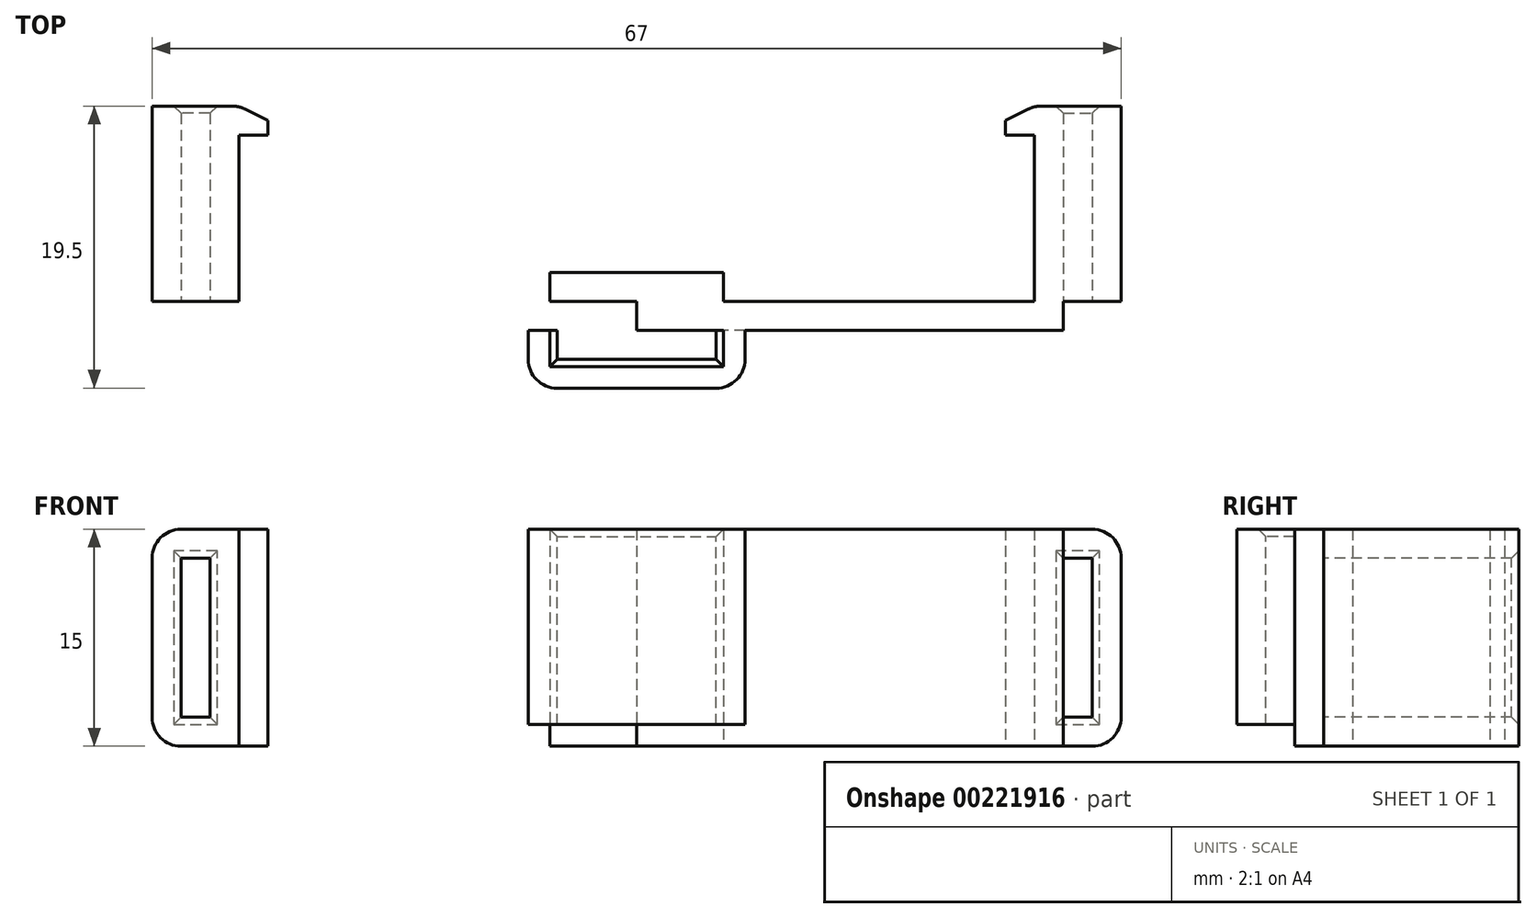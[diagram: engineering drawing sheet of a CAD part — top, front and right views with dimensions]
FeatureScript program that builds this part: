
annotation { "Feature Type Name" : "Feature", "Feature Type Description" : "" }
export const myFeature = defineFeature(function(context is Context, id is Id, definition is map)
    precondition{}
    {
        {
            var Q0;
            Q0=qCreatedBy(makeId("Top.planeOp"),FACE);
            var sketch = newSketch(context, id + "F0", { "sketchPlane" : qUnion([Q0])});
            skLineSegment(sketch, "E0.bottom", {"start": v(27.5, -1) * mm, "end": v(-27.5, -1) * mm});
            skLineSegment(sketch, "E0.top", {"start": v(27.5, 1) * mm, "end": v(-27.5, 1) * mm});
            skLineSegment(sketch, "E0.left", {"start": v(27.5, -1) * mm, "end": v(27.5, 1) * mm});
            skLineSegment(sketch, "E0.right", {"start": v(-27.5, -1) * mm, "end": v(-27.5, 1) * mm});
            skPoint(sketch, "E0.middle", {"position": v(0, 0) * mm});
            skLineSegment(sketch, "E1.bottom", {"start": v(-27.5, -1) * mm, "end": v(-29.5, -1) * mm});
            skLineSegment(sketch, "E1.top", {"start": v(-27.5, 10.5) * mm, "end": v(-29.5, 10.5) * mm});
            skLineSegment(sketch, "E1.left", {"start": v(-27.5, -1) * mm, "end": v(-27.5, 10.5) * mm});
            skLineSegment(sketch, "E1.right", {"start": v(-29.5, -1) * mm, "end": v(-29.5, 10.5) * mm});
            skLineSegment(sketch, "E2.bottom", {"start": v(27.5, -1) * mm, "end": v(29.5, -1) * mm});
            skLineSegment(sketch, "E2.top", {"start": v(27.5, 10.5) * mm, "end": v(29.5, 10.5) * mm});
            skLineSegment(sketch, "E2.left", {"start": v(27.5, -1) * mm, "end": v(27.5, 10.5) * mm});
            skLineSegment(sketch, "E2.right", {"start": v(29.5, -1) * mm, "end": v(29.5, 10.5) * mm});
            skLineSegment(sketch, "E3", {"start": v(27.5, 1) * mm, "end": v(27.5, 10.5) * mm});
            skLineSegment(sketch, "E4", {"start": v(-27.5, 1) * mm, "end": v(-27.5, 10.5) * mm});
            skLineSegment(sketch, "E5.bottom", {"start": v(-29.5, 10.5) * mm, "end": v(-25.5, 10.5) * mm});
            skLineSegment(sketch, "E5.top", {"start": v(-29.5, 12.5) * mm, "end": v(-25.5, 12.5) * mm});
            skLineSegment(sketch, "E5.left", {"start": v(-29.5, 10.5) * mm, "end": v(-29.5, 12.5) * mm});
            skLineSegment(sketch, "E5.right", {"start": v(-25.5, 10.5) * mm, "end": v(-25.5, 12.5) * mm});
            skLineSegment(sketch, "E6.bottom", {"start": v(29.5, 10.5) * mm, "end": v(25.5, 10.5) * mm});
            skLineSegment(sketch, "E6.top", {"start": v(29.5, 12.5) * mm, "end": v(25.5, 12.5) * mm});
            skLineSegment(sketch, "E6.left", {"start": v(29.5, 10.5) * mm, "end": v(29.5, 12.5) * mm});
            skLineSegment(sketch, "E6.right", {"start": v(25.5, 10.5) * mm, "end": v(25.5, 12.5) * mm});
            skLineSegment(sketch, "E7", {"start": v(-25.5, 11.5) * mm, "end": v(-27.5, 12.5) * mm});
            skLineSegment(sketch, "E8", {"start": v(25.5, 11.5) * mm, "end": v(27.5, 12.5) * mm});
            skLineSegment(sketch, "E9", {"start": v(0, 0) * mm, "end": v(0, 17.19) * mm, "construction": true});
            skPoint(sketch, "E9.endSnap0", {"position": v(0, 1) * mm});
            skLineSegment(sketch, "E10.bottom", {"start": v(-29.5, 12.5) * mm, "end": v(-33.5, 12.5) * mm});
            skLineSegment(sketch, "E10.top", {"start": v(-29.5, -1) * mm, "end": v(-33.5, -1) * mm});
            skLineSegment(sketch, "E10.left", {"start": v(-29.5, 12.5) * mm, "end": v(-29.5, -1) * mm});
            skLineSegment(sketch, "E10.right", {"start": v(-33.5, 12.5) * mm, "end": v(-33.5, -1) * mm});
            skLineSegment(sketch, "E11.MirrorCS", {"start": v(33.5, 12.5) * mm, "end": v(33.5, -1) * mm});
            skLineSegment(sketch, "E12.MirrorCS", {"start": v(29.5, 12.5) * mm, "end": v(29.5, -1) * mm});
            skLineSegment(sketch, "E13.MirrorCS", {"start": v(29.5, -1) * mm, "end": v(33.5, -1) * mm});
            skLineSegment(sketch, "E14.MirrorCS", {"start": v(29.5, 12.5) * mm, "end": v(33.5, 12.5) * mm});
            skPoint(sketch, "E15.oppositeSnap0", {"position": v(0, -1) * mm});
            skLineSegment(sketch, "E15.bottom", {"start": v(-29.5, -1) * mm, "end": v(0, -1) * mm});
            skLineSegment(sketch, "E15.top", {"start": v(-29.5, -3) * mm, "end": v(0, -3) * mm});
            skLineSegment(sketch, "E15.left", {"start": v(-29.5, -1) * mm, "end": v(-29.5, -3) * mm});
            skLineSegment(sketch, "E15.right", {"start": v(0, -1) * mm, "end": v(0, -3) * mm});
            skLineSegment(sketch, "E16.MirrorCS", {"start": v(-27.5, -1) * mm, "end": v(27.5, -1) * mm});
            skLineSegment(sketch, "E17.MirrorCS", {"start": v(29.5, -3) * mm, "end": v(0, -3) * mm});
            skLineSegment(sketch, "E18.MirrorCS", {"start": v(29.5, -1) * mm, "end": v(29.5, -3) * mm});
            skLineSegment(sketch, "E19.MirrorCS", {"start": v(29.5, -1) * mm, "end": v(0, -1) * mm});
            skLineSegment(sketch, "E20.bottom", {"start": v(-22, 1) * mm, "end": v(-6, 1) * mm});
            skLineSegment(sketch, "E20.top", {"start": v(-22, -1) * mm, "end": v(-6, -1) * mm});
            skLineSegment(sketch, "E20.left", {"start": v(-22, 1) * mm, "end": v(-22, -1) * mm});
            skLineSegment(sketch, "E20.right", {"start": v(-6, 1) * mm, "end": v(-6, -1) * mm});
            skLineSegment(sketch, "E21.MirrorCS", {"start": v(22, 1) * mm, "end": v(22, -1) * mm});
            skLineSegment(sketch, "E22.MirrorCS", {"start": v(22, 1) * mm, "end": v(6, 1) * mm});
            skLineSegment(sketch, "E23.MirrorCS", {"start": v(6, 1) * mm, "end": v(6, -1) * mm});
            skLineSegment(sketch, "E24.MirrorCS", {"start": v(22, -1) * mm, "end": v(6, -1) * mm});
            skSolve(sketch);
        }
        {
            var Q0;
            Q0=makeQuery(id+"F0.imprint","IMPRINT",FACE,{"disambiguationData":[TD([[makeQuery(id+"F0.imprint","IMPRINT",EDGE,{"derivedFrom":sQuery(id+"F0.wireOp",EDGE,"E0.bottom")}),-1.0]])]});
            var Q1;
            Q1=makeQuery(id+"F0.imprint","IMPRINT",FACE,{"disambiguationData":[TD([[makeQuery(id+"F0.imprint","IMPRINT",EDGE,{"derivedFrom":sQuery(id+"F0.wireOp",EDGE,"E1.bottom")}),-1.0]])]});
            var Q2;
            Q2=makeQuery(id+"F0.imprint","IMPRINT",FACE,{"disambiguationData":[TD([[makeQuery(id+"F0.imprint","IMPRINT",EDGE,{"derivedFrom":sQuery(id+"F0.wireOp",EDGE,"E2.bottom")}),1.0]])]});
            var Q3;
            {var subQ0=sQuery(id+"F0.wireOp",EDGE,"E5.left");Q3=makeQuery(id+"F0.imprint","IMPRINT",FACE,{"disambiguationData":[TD([[makeQuery(id+"F0.imprint","IMPRINT",EDGE,{"derivedFrom":subQ0}),-1.0]])]});}
            var Q4;
            {var subQ0=sQuery(id+"F0.wireOp",EDGE,"E6.left");Q4=makeQuery(id+"F0.imprint","IMPRINT",FACE,{"disambiguationData":[TD([[makeQuery(id+"F0.imprint","IMPRINT",EDGE,{"derivedFrom":subQ0}),1.0]])]});}
            var Q5;
            {var subQ3=sQuery(id+"F0.wireOp",EDGE,"E10.bottom");Q5=makeQuery(id+"F0.imprint","IMPRINT",FACE,{"disambiguationData":[TD([[makeQuery(id+"F0.imprint","IMPRINT",EDGE,{"derivedFrom":subQ3}),1.0]])]});}
            var Q6;
            {var subQ3=sQuery(id+"F0.wireOp",EDGE,"E7");Q6=makeQuery(id+"F0.imprint","IMPRINT",FACE,{"disambiguationData":[TD([[makeQuery(id+"F0.imprint","IMPRINT",EDGE,{"derivedFrom":subQ3}),1.0]])]});}
            var Q7;
            {var subQ3=sQuery(id+"F0.wireOp",EDGE,"E8");Q7=makeQuery(id+"F0.imprint","IMPRINT",FACE,{"disambiguationData":[TD([[makeQuery(id+"F0.imprint","IMPRINT",EDGE,{"derivedFrom":subQ3}),-1.0]])]});}
            var Q8;
            Q8=makeQuery(id+"F0.imprint","IMPRINT",FACE,{"disambiguationData":[TD([[makeQuery(id+"F0.imprint","IMPRINT",EDGE,{"derivedFrom":sQuery(id+"F0.wireOp",EDGE,"E11.MirrorCS")}),-1.0]])]});
            var Q9;
            Q9=makeQuery(id+"F0.imprint","IMPRINT",FACE,{"disambiguationData":[TD([[makeQuery(id+"F0.imprint","IMPRINT",EDGE,{"derivedFrom":sQuery(id+"F0.wireOp",EDGE,"E1.left")}),1.0]])]});
            var Q10;
            {var subQ3=sQuery(id+"F0.wireOp",EDGE,"E2.left");Q10=makeQuery(id+"F0.imprint","IMPRINT",FACE,{"disambiguationData":[TD([[makeQuery(id+"F0.imprint","IMPRINT",EDGE,{"derivedFrom":subQ3}),-1.0]])]});}
            var Q11;
            {var subQ0=sQuery(id+"F0.wireOp",EDGE,"E2.left");Q11=makeQuery(id+"F0.imprint","IMPRINT",FACE,{"disambiguationData":[TD([[makeQuery(id+"F0.imprint","IMPRINT",EDGE,{"derivedFrom":subQ0}),1.0]])]});}
            var Q12;
            {var subQ3=sQuery(id+"F0.wireOp",EDGE,"E15.right");Q12=makeQuery(id+"F0.imprint","IMPRINT",FACE,{"disambiguationData":[TD([[makeQuery(id+"F0.imprint","IMPRINT",EDGE,{"derivedFrom":subQ3}),1.0]])]});}
            var Q13;
            {var subQ0=sQuery(id+"F0.wireOp",EDGE,"E20.right");Q13=makeQuery(id+"F0.imprint","IMPRINT",FACE,{"disambiguationData":[TD([[makeQuery(id+"F0.imprint","IMPRINT",EDGE,{"derivedFrom":subQ0}),1.0]])]});}
            var Q14;
            {var subQ1=sQuery(id+"F0.wireOp",EDGE,"E15.bottom");Q14=makeQuery(id+"F0.imprint","IMPRINT",FACE,{"disambiguationData":[TD([[makeQuery(id+"F0.imprint","IMPRINT",EDGE,{"derivedFrom":subQ1}),-1.0]])]});}
            var Q15;
            {var subQ0=sQuery(id+"F0.wireOp",EDGE,"E1.left");Q15=makeQuery(id+"F0.imprint","IMPRINT",FACE,{"disambiguationData":[TD([[makeQuery(id+"F0.imprint","IMPRINT",EDGE,{"derivedFrom":subQ0}),-1.0]])]});}
            extrude(context, id + "F1", {"entities" : qUnion([Q0, Q1, Q2, Q3, Q4, Q5, Q6, Q7, Q8, Q9, Q10, Q11, Q12, Q13, Q14, Q15]), "depth" : 15 * mm});
        }
        {
            var Q0;
            Q0=makeQuery(id+"F1.opExtrude","SWEPT_FACE",FACE,{"disambiguationData":[OSD([sQuery(id+"F0.wireOp",EDGE,"E0.bottom"),sQuery(id+"F0.wireOp",EDGE,"E1.bottom"),sQuery(id+"F0.wireOp",EDGE,"E2.bottom"),sQuery(id+"F0.wireOp",EDGE,"E10.top"),sQuery(id+"F0.wireOp",EDGE,"E13.MirrorCS")])]});
            var sketch = newSketch(context, id + "F2", { "sketchPlane" : qUnion([Q0])});
            skLineSegment(sketch, "E25", {"start": v(-31.5, 0) * mm, "end": v(-31.5, 15) * mm, "construction": true});
            skLineSegment(sketch, "E26.bottom", {"start": v(-31.5, 13) * mm, "end": v(-29.5, 13) * mm});
            skLineSegment(sketch, "E26.top", {"start": v(-31.5, 2) * mm, "end": v(-29.5, 2) * mm});
            skLineSegment(sketch, "E26.left", {"start": v(-31.5, 13) * mm, "end": v(-31.5, 2) * mm});
            skLineSegment(sketch, "E26.right", {"start": v(-29.5, 13) * mm, "end": v(-29.5, 2) * mm});
            skLineSegment(sketch, "E27.MirrorCS", {"start": v(-31.5, 13) * mm, "end": v(-33.5, 13) * mm});
            skLineSegment(sketch, "E28.MirrorCS", {"start": v(-33.5, 13) * mm, "end": v(-33.5, 2) * mm});
            skLineSegment(sketch, "E29.MirrorCS", {"start": v(-31.5, 2) * mm, "end": v(-33.5, 2) * mm});
            skLineSegment(sketch, "E30", {"start": v(-31.5, 13) * mm, "end": v(-33.5, 13) * mm, "construction": true});
            skLineSegment(sketch, "E31", {"start": v(-31.5, 13) * mm, "end": v(-31.5, 15) * mm, "construction": true});
            skLineSegment(sketch, "E32", {"start": v(-31.5, 2) * mm, "end": v(-31.5, 0) * mm, "construction": true});
            skLineSegment(sketch, "E33.MirrorCS", {"start": v(31.5, 2) * mm, "end": v(31.5, 0) * mm, "construction": true});
            skLineSegment(sketch, "E34.MirrorCS", {"start": v(31.5, 13) * mm, "end": v(29.5, 13) * mm});
            skLineSegment(sketch, "E35.MirrorCS", {"start": v(31.5, 2) * mm, "end": v(33.5, 2) * mm});
            skLineSegment(sketch, "E36.MirrorCS", {"start": v(31.5, 13) * mm, "end": v(31.5, 15) * mm, "construction": true});
            skLineSegment(sketch, "E37.MirrorCS", {"start": v(31.5, 13) * mm, "end": v(31.5, 2) * mm});
            skLineSegment(sketch, "E38.MirrorCS", {"start": v(31.5, 13) * mm, "end": v(33.5, 13) * mm});
            skLineSegment(sketch, "E39.MirrorCS", {"start": v(33.5, 13) * mm, "end": v(33.5, 2) * mm});
            skLineSegment(sketch, "E40.MirrorCS", {"start": v(31.5, 2) * mm, "end": v(29.5, 2) * mm});
            skLineSegment(sketch, "E41.MirrorCS", {"start": v(31.5, 13) * mm, "end": v(33.5, 13) * mm, "construction": true});
            skLineSegment(sketch, "E42.MirrorCS", {"start": v(31.5, 0) * mm, "end": v(31.5, 15) * mm, "construction": true});
            skLineSegment(sketch, "E43.MirrorCS", {"start": v(29.5, 13) * mm, "end": v(29.5, 2) * mm});
            skSolve(sketch);
        }
        {
            var Q0;
            Q0=makeQuery(id+"F2.imprint","IMPRINT",FACE,{"disambiguationData":[TD([[makeQuery(id+"F2.imprint","IMPRINT",EDGE,{"derivedFrom":sQuery(id+"F2.wireOp",EDGE,"E26.bottom")}),-1.0]])]});
            var Q1;
            Q1=makeQuery(id+"F2.imprint","IMPRINT",FACE,{"disambiguationData":[TD([[makeQuery(id+"F2.imprint","IMPRINT",EDGE,{"derivedFrom":sQuery(id+"F2.wireOp",EDGE,"E34.MirrorCS")}),1.0]])]});
            extrude(context, id + "F3", {"entities" : qUnion([Q0, Q1]), "operationType" : NewBodyOperationType.REMOVE, "endBound" : BoundingType.THROUGH_ALL, "oppositeDirection" : true, "depth" : 25 * mm});
        }
        {
            var Q0;
            Q0=makeQuery(id+"F1.opExtrude","CAP_FACE",FACE,{"disambiguationData":[OSD([sQuery(id+"F0.wireOp",EDGE,"E0.top"),sQuery(id+"F0.wireOp",EDGE,"E3"),sQuery(id+"F0.wireOp",EDGE,"E4"),sQuery(id+"F0.wireOp",EDGE,"E5.bottom"),sQuery(id+"F0.wireOp",EDGE,"E5.top"),sQuery(id+"F0.wireOp",EDGE,"E5.right"),sQuery(id+"F0.wireOp",EDGE,"E6.bottom"),sQuery(id+"F0.wireOp",EDGE,"E6.top"),sQuery(id+"F0.wireOp",EDGE,"E6.right"),sQuery(id+"F0.wireOp",EDGE,"E7"),sQuery(id+"F0.wireOp",EDGE,"E8"),sQuery(id+"F0.wireOp",EDGE,"E10.bottom"),sQuery(id+"F0.wireOp",EDGE,"E10.top"),sQuery(id+"F0.wireOp",EDGE,"E10.right"),sQuery(id+"F0.wireOp",EDGE,"E11.MirrorCS"),sQuery(id+"F0.wireOp",EDGE,"E13.MirrorCS"),sQuery(id+"F0.wireOp",EDGE,"E14.MirrorCS"),sQuery(id+"F0.wireOp",EDGE,"E15.top"),sQuery(id+"F0.wireOp",EDGE,"E15.left"),sQuery(id+"F0.wireOp",EDGE,"E17.MirrorCS"),sQuery(id+"F0.wireOp",EDGE,"E18.MirrorCS"),sQuery(id+"F0.wireOp",EDGE,"E20.top"),sQuery(id+"F0.wireOp",EDGE,"E20.left"),sQuery(id+"F0.wireOp",EDGE,"E20.right"),sQuery(id+"F0.wireOp",EDGE,"E21.MirrorCS"),sQuery(id+"F0.wireOp",EDGE,"E23.MirrorCS"),sQuery(id+"F0.wireOp",EDGE,"E24.MirrorCS")])],"isStart":false});
            var sketch = newSketch(context, id + "F4", { "sketchPlane" : qUnion([Q0])});
            skLineSegment(sketch, "E44.bottom", {"start": v(7.5, -3) * mm, "end": v(-7.5, -3) * mm});
            skLineSegment(sketch, "E44.top", {"start": v(7.5, -7) * mm, "end": v(-7.5, -7) * mm});
            skLineSegment(sketch, "E44.left", {"start": v(7.5, -3) * mm, "end": v(7.5, -7) * mm});
            skLineSegment(sketch, "E44.right", {"start": v(-7.5, -3) * mm, "end": v(-7.5, -7) * mm});
            skPoint(sketch, "E45", {"position": v(0, -3) * mm});
            skLineSegment(sketch, "E46.bottom", {"start": v(-5.5, -3) * mm, "end": v(5.5, -3) * mm});
            skLineSegment(sketch, "E46.top", {"start": v(-5.5, -5) * mm, "end": v(5.5, -5) * mm});
            skLineSegment(sketch, "E46.left", {"start": v(-5.5, -3) * mm, "end": v(-5.5, -5) * mm});
            skLineSegment(sketch, "E46.right", {"start": v(5.5, -3) * mm, "end": v(5.5, -5) * mm});
            skLineSegment(sketch, "E47", {"start": v(-5.5, -5) * mm, "end": v(-7.5, -5) * mm});
            skLineSegment(sketch, "E48", {"start": v(-7.5, -5) * mm, "end": v(-5.5, -5) * mm, "construction": true});
            skLineSegment(sketch, "E49", {"start": v(-5.5, -5) * mm, "end": v(-5.5, -7) * mm, "construction": true});
            skSolve(sketch);
        }
        {
            var Q0;
            {var subQ3=sQuery(id+"F4.wireOp",EDGE,"E46.left");Q0=makeQuery(id+"F4.imprint","IMPRINT",FACE,{"disambiguationData":[TD([[makeQuery(id+"F4.imprint","IMPRINT",EDGE,{"derivedFrom":subQ3}),-1.0]])]});}
            var Q1;
            {var subQ1=sQuery(id+"F4.wireOp",EDGE,"E44.top");Q1=makeQuery(id+"F4.imprint","IMPRINT",FACE,{"disambiguationData":[TD([[makeQuery(id+"F4.imprint","IMPRINT",EDGE,{"derivedFrom":subQ1}),-1.0]])]});}
            extrude(context, id + "F5", {"entities" : qUnion([Q0, Q1]), "operationType" : NewBodyOperationType.ADD, "oppositeDirection" : true, "depth" : 13.5 * mm});
        }
        {
            var Q0;
            Q0=makeQuery(id+"F1.opExtrude","CAP_EDGE",EDGE,{"disambiguationData":[OSD([sQuery(id+"F0.wireOp",EDGE,"E11.MirrorCS")])],"isStart":false});
            var Q1;
            Q1=makeQuery(id+"F1.opExtrude","CAP_EDGE",EDGE,{"disambiguationData":[OSD([sQuery(id+"F0.wireOp",EDGE,"E10.right")])],"isStart":false});
            var Q2;
            Q2=makeQuery(id+"F1.opExtrude","CAP_EDGE",EDGE,{"disambiguationData":[OSD([sQuery(id+"F0.wireOp",EDGE,"E11.MirrorCS")])],"isStart":true});
            var Q3;
            Q3=makeQuery(id+"F1.opExtrude","CAP_EDGE",EDGE,{"disambiguationData":[OSD([sQuery(id+"F0.wireOp",EDGE,"E10.right")])],"isStart":true});
            var Q4;
            Q4=makeQuery(id+"F1.opExtrude","SWEPT_EDGE",EDGE,{"disambiguationData":[OSD([sQuery(id+"F0.wireOp",EDGE,"E5.top"),sQuery(id+"F0.wireOp",EDGE,"E7")])]});
            var Q5;
            Q5=makeQuery(id+"F1.opExtrude","SWEPT_EDGE",EDGE,{"disambiguationData":[OSD([sQuery(id+"F0.wireOp",EDGE,"E6.top"),sQuery(id+"F0.wireOp",EDGE,"E8")])]});
            var Q6;
            Q6=makeQuery(id+"F5.opExtrude","SWEPT_EDGE",EDGE,{"disambiguationData":[OSD([sQuery(id+"F4.wireOp",EDGE,"E44.top"),sQuery(id+"F4.wireOp",EDGE,"E44.right")])]});
            var Q7;
            Q7=makeQuery(id+"F5.opExtrude","SWEPT_EDGE",EDGE,{"disambiguationData":[OSD([sQuery(id+"F4.wireOp",EDGE,"E44.top"),sQuery(id+"F4.wireOp",EDGE,"E44.left")])]});
            fillet(context, id + "F6", {"entities" : qUnion([Q0, Q1, Q2, Q3, Q4, Q5, Q6, Q7]), "radius" : 2 * mm, "tangentPropagation" : true, "allowEdgeOverflow" : false});
        }
        {
            var Q0;
            Q0=makeQuery(id+"F3.boolean.opBoolean","COPY",EDGE,{"derivedFrom":makeQuery(id+"F3.opExtrude","CAP_EDGE",EDGE,{"disambiguationData":[OSD([sQuery(id+"F2.wireOp",EDGE,"E26.left")])],"isStart":true})});
            var Q1;
            Q1=makeQuery(id+"F3.boolean.opBoolean","COPY",EDGE,{"derivedFrom":makeQuery(id+"F3.opExtrude","CAP_EDGE",EDGE,{"disambiguationData":[OSD([sQuery(id+"F2.wireOp",EDGE,"E28.MirrorCS")])],"isStart":true})});
            var Q2;
            Q2=makeQuery(id+"F3.boolean.opBoolean","COPY",EDGE,{"derivedFrom":makeQuery(id+"F3.opExtrude","CAP_EDGE",EDGE,{"disambiguationData":[OSD([sQuery(id+"F2.wireOp",EDGE,"E27.MirrorCS")])],"isStart":true})});
            var Q3;
            Q3=makeQuery(id+"F3.boolean.opBoolean","COPY",EDGE,{"derivedFrom":makeQuery(id+"F3.opExtrude","CAP_EDGE",EDGE,{"disambiguationData":[OSD([sQuery(id+"F2.wireOp",EDGE,"E29.MirrorCS")])],"isStart":true})});
            var Q4;
            Q4=makeQuery(id+"F3.boolean.opBoolean","COPY",EDGE,{"derivedFrom":makeQuery(id+"F3.opExtrude","CAP_EDGE",EDGE,{"disambiguationData":[OSD([sQuery(id+"F2.wireOp",EDGE,"E26.right")])],"isStart":true})});
            var Q5;
            Q5=makeQuery(id+"F3.boolean.opBoolean","COPY",EDGE,{"derivedFrom":makeQuery(id+"F3.opExtrude","CAP_EDGE",EDGE,{"disambiguationData":[OSD([sQuery(id+"F2.wireOp",EDGE,"E26.bottom")])],"isStart":true})});
            var Q6;
            Q6=makeQuery(id+"F3.boolean.opBoolean","COPY",EDGE,{"derivedFrom":makeQuery(id+"F3.opExtrude","CAP_EDGE",EDGE,{"disambiguationData":[OSD([sQuery(id+"F2.wireOp",EDGE,"E26.left")])],"isStart":true})});
            var Q7;
            Q7=makeQuery(id+"F3.boolean.opBoolean","COPY",EDGE,{"derivedFrom":makeQuery(id+"F3.opExtrude","CAP_EDGE",EDGE,{"disambiguationData":[OSD([sQuery(id+"F2.wireOp",EDGE,"E26.top")])],"isStart":true})});
            var Q8;
            Q8=makeQuery(id+"F3.boolean.opBoolean","COPY",EDGE,{"derivedFrom":makeQuery(id+"F3.opExtrude","CAP_EDGE",EDGE,{"disambiguationData":[OSD([sQuery(id+"F2.wireOp",EDGE,"E37.MirrorCS")])],"isStart":true})});
            var Q9;
            Q9=makeQuery(id+"F3.boolean.opBoolean","COPY",EDGE,{"derivedFrom":makeQuery(id+"F3.opExtrude","CAP_EDGE",EDGE,{"disambiguationData":[OSD([sQuery(id+"F2.wireOp",EDGE,"E34.MirrorCS")])],"isStart":true})});
            var Q10;
            Q10=makeQuery(id+"F3.boolean.opBoolean","COPY",EDGE,{"derivedFrom":makeQuery(id+"F3.opExtrude","CAP_EDGE",EDGE,{"disambiguationData":[OSD([sQuery(id+"F2.wireOp",EDGE,"E40.MirrorCS")])],"isStart":true})});
            var Q11;
            Q11=makeQuery(id+"F3.boolean.opBoolean","INTERSECT",EDGE,{"derivedFrom":[makeQuery(id+"F1.opExtrude","SWEPT_FACE",FACE,{"disambiguationData":[OSD([sQuery(id+"F0.wireOp",EDGE,"E6.top"),sQuery(id+"F0.wireOp",EDGE,"E14.MirrorCS")])]}),makeQuery(id+"F3.opExtrude","SWEPT_FACE",FACE,{"disambiguationData":[OSD([sQuery(id+"F2.wireOp",EDGE,"E37.MirrorCS")])]})]});
            var Q12;
            Q12=makeQuery(id+"F3.boolean.opBoolean","INTERSECT",EDGE,{"derivedFrom":[makeQuery(id+"F1.opExtrude","SWEPT_FACE",FACE,{"disambiguationData":[OSD([sQuery(id+"F0.wireOp",EDGE,"E6.top"),sQuery(id+"F0.wireOp",EDGE,"E14.MirrorCS")])]}),makeQuery(id+"F3.opExtrude","SWEPT_FACE",FACE,{"disambiguationData":[OSD([sQuery(id+"F2.wireOp",EDGE,"E40.MirrorCS")])]})]});
            var Q13;
            Q13=makeQuery(id+"F3.boolean.opBoolean","INTERSECT",EDGE,{"derivedFrom":[makeQuery(id+"F1.opExtrude","SWEPT_FACE",FACE,{"disambiguationData":[OSD([sQuery(id+"F0.wireOp",EDGE,"E6.top"),sQuery(id+"F0.wireOp",EDGE,"E14.MirrorCS")])]}),makeQuery(id+"F3.opExtrude","SWEPT_FACE",FACE,{"disambiguationData":[OSD([sQuery(id+"F2.wireOp",EDGE,"E43.MirrorCS")])]})]});
            var Q14;
            Q14=makeQuery(id+"F3.boolean.opBoolean","INTERSECT",EDGE,{"derivedFrom":[makeQuery(id+"F1.opExtrude","SWEPT_FACE",FACE,{"disambiguationData":[OSD([sQuery(id+"F0.wireOp",EDGE,"E6.top"),sQuery(id+"F0.wireOp",EDGE,"E14.MirrorCS")])]}),makeQuery(id+"F3.opExtrude","SWEPT_FACE",FACE,{"disambiguationData":[OSD([sQuery(id+"F2.wireOp",EDGE,"E34.MirrorCS")])]})]});
            var Q15;
            Q15=makeQuery(id+"F3.boolean.opBoolean","INTERSECT",EDGE,{"derivedFrom":[makeQuery(id+"F1.opExtrude","SWEPT_FACE",FACE,{"disambiguationData":[OSD([sQuery(id+"F0.wireOp",EDGE,"E5.top"),sQuery(id+"F0.wireOp",EDGE,"E10.bottom")])]}),makeQuery(id+"F3.opExtrude","SWEPT_FACE",FACE,{"disambiguationData":[OSD([sQuery(id+"F2.wireOp",EDGE,"E26.top")])]})]});
            var Q16;
            Q16=makeQuery(id+"F3.boolean.opBoolean","INTERSECT",EDGE,{"derivedFrom":[makeQuery(id+"F1.opExtrude","SWEPT_FACE",FACE,{"disambiguationData":[OSD([sQuery(id+"F0.wireOp",EDGE,"E5.top"),sQuery(id+"F0.wireOp",EDGE,"E10.bottom")])]}),makeQuery(id+"F3.opExtrude","SWEPT_FACE",FACE,{"disambiguationData":[OSD([sQuery(id+"F2.wireOp",EDGE,"E26.right")])]})]});
            var Q17;
            Q17=makeQuery(id+"F3.boolean.opBoolean","INTERSECT",EDGE,{"derivedFrom":[makeQuery(id+"F1.opExtrude","SWEPT_FACE",FACE,{"disambiguationData":[OSD([sQuery(id+"F0.wireOp",EDGE,"E5.top"),sQuery(id+"F0.wireOp",EDGE,"E10.bottom")])]}),makeQuery(id+"F3.opExtrude","SWEPT_FACE",FACE,{"disambiguationData":[OSD([sQuery(id+"F2.wireOp",EDGE,"E26.left")])]})]});
            var Q18;
            Q18=makeQuery(id+"F3.boolean.opBoolean","INTERSECT",EDGE,{"derivedFrom":[makeQuery(id+"F1.opExtrude","SWEPT_FACE",FACE,{"disambiguationData":[OSD([sQuery(id+"F0.wireOp",EDGE,"E5.top"),sQuery(id+"F0.wireOp",EDGE,"E10.bottom")])]}),makeQuery(id+"F3.opExtrude","SWEPT_FACE",FACE,{"disambiguationData":[OSD([sQuery(id+"F2.wireOp",EDGE,"E26.bottom")])]})]});
            var Q19;
            {var subQ0=sQuery(id+"F4.wireOp",EDGE,"E46.left");var subQ2=sQuery(id+"F0.wireOp",EDGE,"E17.MirrorCS");var subQ3=sQuery(id+"F0.wireOp",EDGE,"E15.top");Q19=makeQuery(id+"F5.boolean.opBoolean","SPLIT",EDGE,{"disambiguationData":[TD([makeQuery(id+"F5.opExtrude","SWEPT_FACE",FACE,{"disambiguationData":[OSD([subQ0])]})])],"derivedFrom":makeQuery(id+"F1.opExtrude","CAP_EDGE",EDGE,{"disambiguationData":[OSD([subQ3,subQ2])],"isStart":false})});}
            var Q20;
            Q20=makeQuery(id+"F5.opExtrude","CAP_EDGE",EDGE,{"disambiguationData":[OSD([sQuery(id+"F4.wireOp",EDGE,"E46.left")])],"isStart":true});
            var Q21;
            Q21=makeQuery(id+"F5.opExtrude","CAP_EDGE",EDGE,{"disambiguationData":[OSD([sQuery(id+"F4.wireOp",EDGE,"E46.top")])],"isStart":true});
            var Q22;
            Q22=makeQuery(id+"F5.opExtrude","CAP_EDGE",EDGE,{"disambiguationData":[OSD([sQuery(id+"F4.wireOp",EDGE,"E46.right")])],"isStart":true});
            chamfer(context, id + "F7", {"entities" : qUnion([Q0, Q1, Q2, Q3, Q4, Q5, Q6, Q7, Q8, Q9, Q10, Q11, Q12, Q13, Q14, Q15, Q16, Q17, Q18, Q19, Q20, Q21, Q22]), "width" : 0.5 * mm, "tangentPropagation" : true});
        }
    });
